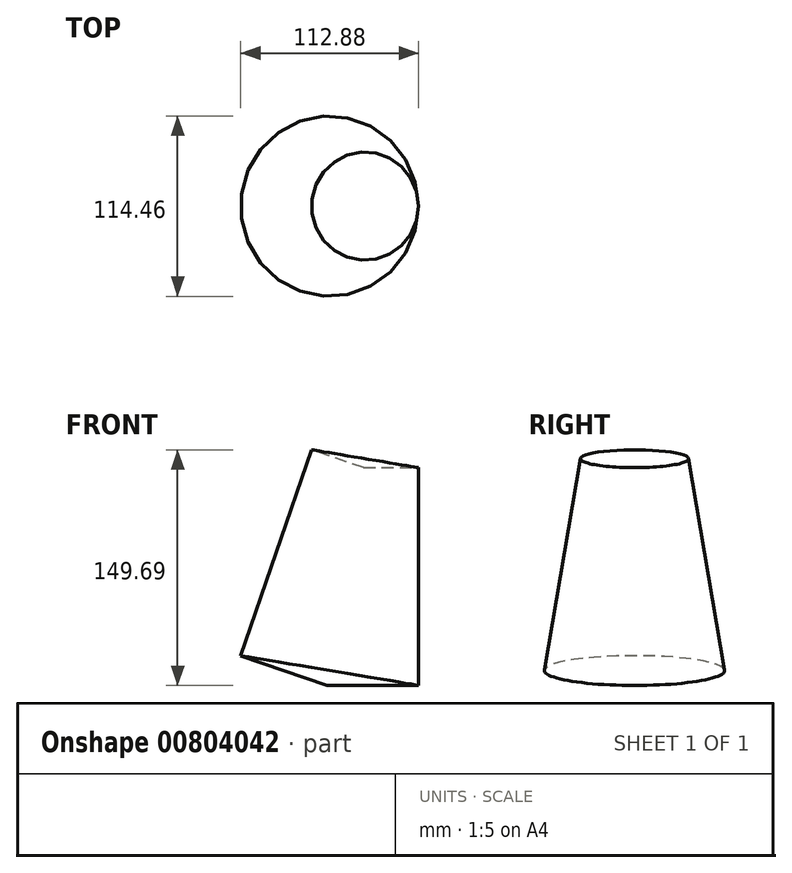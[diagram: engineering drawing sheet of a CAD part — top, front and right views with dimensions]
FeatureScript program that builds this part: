
annotation { "Feature Type Name" : "Feature", "Feature Type Description" : "" }
export const myFeature = defineFeature(function(context is Context, id is Id, definition is map)
    precondition{}
    {
        {
            var Q0;
            Q0=qCreatedBy(makeId("Front.planeOp"),FACE);
            var sketch = newSketch(context, id + "F0", { "sketchPlane" : qUnion([Q0])});
            skLineSegment(sketch, "E0.bottom", {"start": v(-33.74, 69.17) * mm, "end": v(33.74, 69.17) * mm});
            skLineSegment(sketch, "E0.top", {"start": v(-33.74, -69.17) * mm, "end": v(33.74, -69.17) * mm});
            skLineSegment(sketch, "E0.left", {"start": v(-33.74, 69.17) * mm, "end": v(-33.74, -69.17) * mm});
            skLineSegment(sketch, "E0.right", {"start": v(33.74, 69.17) * mm, "end": v(33.74, -69.17) * mm});
            skPoint(sketch, "E0.middle", {"position": v(0, 0) * mm});
            skLineSegment(sketch, "E1", {"start": v(0, 75.89) * mm, "end": v(-24.28, -69.17) * mm});
            skSolve(sketch);
        }
        {
            var Q0;
            {var subQ0=sQuery(id+"F0.wireOp",EDGE,"E0.right");Q0=makeQuery(id+"F0.imprint","IMPRINT",FACE,{"disambiguationData":[TD([[makeQuery(id+"F0.imprint","IMPRINT",EDGE,{"derivedFrom":subQ0}),-1.0]])]});}
            var Q1;
            Q1=sQuery(id+"F0.wireOp",EDGE,"E1");
            revolve(context, id + "F1", {"surfaceOperationType" : NewSurfaceOperationType.NEW, "entities" : qUnion([Q0]), "axis" : qUnion([Q1]), "revolveType" : RevolveType.FULL});
        }
    });
